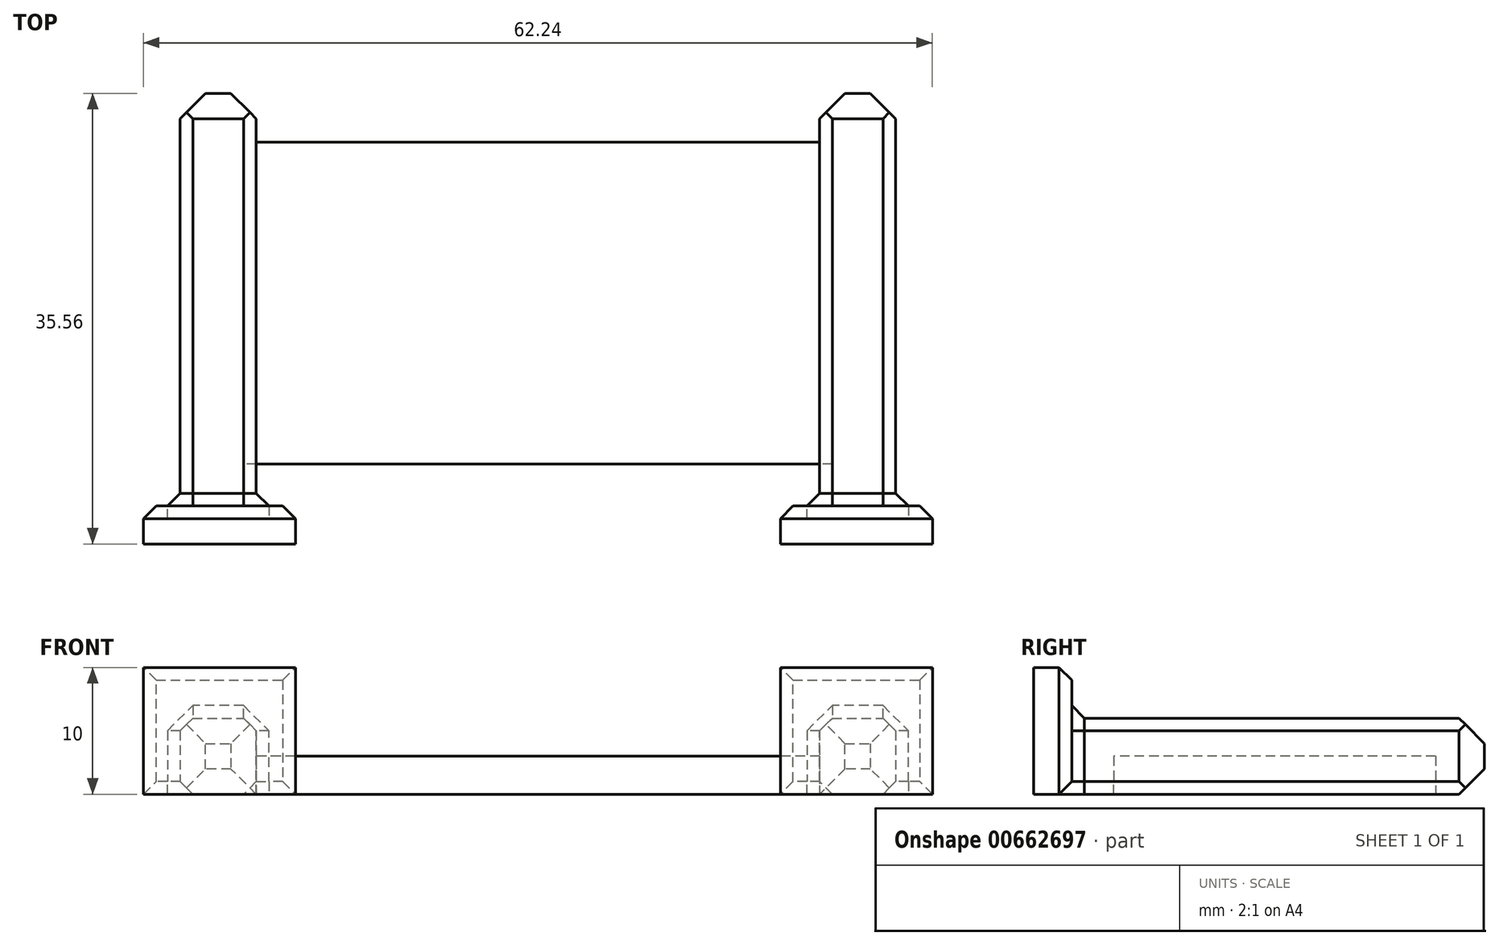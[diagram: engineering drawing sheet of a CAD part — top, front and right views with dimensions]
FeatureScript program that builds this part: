
annotation { "Feature Type Name" : "Feature", "Feature Type Description" : "" }
export const myFeature = defineFeature(function(context is Context, id is Id, definition is map)
    precondition{}
    {
        {
            var Q0;
            Q0=qCreatedBy(makeId("Top.planeOp"),FACE);
            var sketch = newSketch(context, id + "F0", { "sketchPlane" : qUnion([Q0])});
            skLineSegment(sketch, "E0.bottom", {"start": v(0, 0) * mm, "end": v(22.22, 0) * mm});
            skLineSegment(sketch, "E0.right", {"start": v(22.22, 0) * mm, "end": v(22.23, 25.4) * mm});
            skLineSegment(sketch, "E1.bottom", {"start": v(22.23, 29.26) * mm, "end": v(28.22, 29.26) * mm});
            skLineSegment(sketch, "E1.top", {"start": v(22.23, -6.3) * mm, "end": v(28.23, -6.3) * mm});
            skLineSegment(sketch, "E1.left", {"start": v(22.22, 29.26) * mm, "end": v(22.23, -3.3) * mm});
            skLineSegment(sketch, "E1.right", {"start": v(28.22, 29.26) * mm, "end": v(28.23, -3.3) * mm});
            skLineSegment(sketch, "E2.MirrorCS", {"start": v(-28.23, 29.26) * mm, "end": v(-28.23, -3.3) * mm});
            skLineSegment(sketch, "E3.MirrorCS", {"start": v(-22.23, 29.26) * mm, "end": v(-28.22, 29.26) * mm});
            skLineSegment(sketch, "E4.MirrorCS", {"start": v(-22.23, 29.26) * mm, "end": v(-22.23, -3.3) * mm});
            skLineSegment(sketch, "E5.MirrorCS", {"start": v(0, 0) * mm, "end": v(-22.22, 0) * mm});
            skLineSegment(sketch, "E6.MirrorCS", {"start": v(-22.23, -6.3) * mm, "end": v(-28.23, -6.3) * mm});
            skLineSegment(sketch, "E7.bottom", {"start": v(19.12, -6.3) * mm, "end": v(31.12, -6.3) * mm});
            skLineSegment(sketch, "E7.top", {"start": v(19.12, -3.3) * mm, "end": v(31.12, -3.3) * mm});
            skLineSegment(sketch, "E7.left", {"start": v(19.12, -6.3) * mm, "end": v(19.12, -3.3) * mm});
            skLineSegment(sketch, "E7.right", {"start": v(31.12, -6.3) * mm, "end": v(31.12, -3.3) * mm});
            skLineSegment(sketch, "E8.MirrorCS", {"start": v(-19.12, -3.3) * mm, "end": v(-31.12, -3.3) * mm});
            skLineSegment(sketch, "E9.MirrorCS", {"start": v(-19.12, -6.3) * mm, "end": v(-19.12, -3.3) * mm});
            skLineSegment(sketch, "E10.MirrorCS", {"start": v(-19.12, -6.3) * mm, "end": v(-31.12, -6.3) * mm});
            skLineSegment(sketch, "E11.MirrorCS", {"start": v(-31.12, -6.3) * mm, "end": v(-31.12, -3.3) * mm});
            skPoint(sketch, "E12.orphan", {"position": v(-28.23, -6.3) * mm});
            skPoint(sketch, "E13.orphan", {"position": v(-22.23, -6.3) * mm});
            skLineSegment(sketch, "E14", {"start": v(22.23, 25.4) * mm, "end": v(-22.23, 25.4) * mm});
            skSolve(sketch);
        }
        {
            var Q0;
            {var subQ2=sQuery(id+"F0.wireOp",EDGE,"E0.bottom");Q0=makeQuery(id+"F0.imprint","IMPRINT",FACE,{"disambiguationData":[TD([[makeQuery(id+"F0.imprint","IMPRINT",EDGE,{"derivedFrom":subQ2}),1.0]])]});}
            extrude(context, id + "F1", {"entities" : qUnion([Q0]), "depth" : 3 * mm, "offsetDistance" : 25 * mm});
        }
        {
            var Q0;
            {var subQ5=sQuery(id+"F0.wireOp",EDGE,"E2.MirrorCS");Q0=makeQuery(id+"F0.imprint","IMPRINT",FACE,{"disambiguationData":[TD([[makeQuery(id+"F0.imprint","IMPRINT",EDGE,{"derivedFrom":subQ5}),1.0]])]});}
            var Q1;
            {var subQ6=sQuery(id+"F0.wireOp",EDGE,"E1.bottom");Q1=makeQuery(id+"F0.imprint","IMPRINT",FACE,{"disambiguationData":[TD([[makeQuery(id+"F0.imprint","IMPRINT",EDGE,{"derivedFrom":subQ6}),-1.0]])]});}
            extrude(context, id + "F2", {"entities" : qUnion([Q0, Q1]), "operationType" : NewBodyOperationType.ADD, "depth" : 6 * mm, "offsetDistance" : 25 * mm});
        }
        {
            var Q0;
            {var subQ0=sQuery(id+"F0.wireOp",EDGE,"E9.MirrorCS");Q0=makeQuery(id+"F0.imprint","IMPRINT",FACE,{"disambiguationData":[TD([[makeQuery(id+"F0.imprint","IMPRINT",EDGE,{"derivedFrom":subQ0}),1.0]])]});}
            var Q1;
            {var subQ4=sQuery(id+"F0.wireOp",EDGE,"E7.left");Q1=makeQuery(id+"F0.imprint","IMPRINT",FACE,{"disambiguationData":[TD([[makeQuery(id+"F0.imprint","IMPRINT",EDGE,{"derivedFrom":subQ4}),-1.0]])]});}
            extrude(context, id + "F3", {"entities" : qUnion([Q0, Q1]), "operationType" : NewBodyOperationType.ADD, "depth" : 10 * mm, "offsetDistance" : 25 * mm});
        }
        {
            var Q0;
            Q0=makeQuery(id+"F2.opExtrude","SWEPT_FACE",FACE,{"disambiguationData":[OSD([sQuery(id+"F0.wireOp",EDGE,"E3.MirrorCS")])]});
            var Q1;
            Q1=makeQuery(id+"F2.opExtrude","SWEPT_FACE",FACE,{"disambiguationData":[OSD([sQuery(id+"F0.wireOp",EDGE,"E1.bottom")])]});
            chamfer(context, id + "F4", {"entities" : qUnion([Q0, Q1]), "width" : 2 * mm, "tangentPropagation" : true});
        }
        {
            var Q0;
            Q0=makeQuery(id+"F3.opExtrude","SWEPT_FACE",FACE,{"disambiguationData":[OSD([sQuery(id+"F0.wireOp",EDGE,"E8.MirrorCS")])]});
            var Q1;
            Q1=makeQuery(id+"F3.opExtrude","SWEPT_FACE",FACE,{"disambiguationData":[OSD([sQuery(id+"F0.wireOp",EDGE,"E7.top")])]});
            var Q2;
            Q2=makeQuery(id+"F2.opExtrude","CAP_EDGE",EDGE,{"disambiguationData":[OSD([sQuery(id+"F0.wireOp",EDGE,"E4.MirrorCS")])],"isStart":false});
            var Q3;
            Q3=makeQuery(id+"F2.opExtrude","CAP_EDGE",EDGE,{"disambiguationData":[OSD([sQuery(id+"F0.wireOp",EDGE,"E2.MirrorCS")])],"isStart":false});
            var Q4;
            Q4=makeQuery(id+"F2.opExtrude","CAP_EDGE",EDGE,{"disambiguationData":[OSD([sQuery(id+"F0.wireOp",EDGE,"E1.left")])],"isStart":false});
            var Q5;
            Q5=makeQuery(id+"F2.opExtrude","CAP_EDGE",EDGE,{"disambiguationData":[OSD([sQuery(id+"F0.wireOp",EDGE,"E1.right")])],"isStart":false});
            chamfer(context, id + "F5", {"entities" : qUnion([Q0, Q1, Q2, Q3, Q4, Q5]), "width" : 1 * mm, "tangentPropagation" : true});
        }
    });
